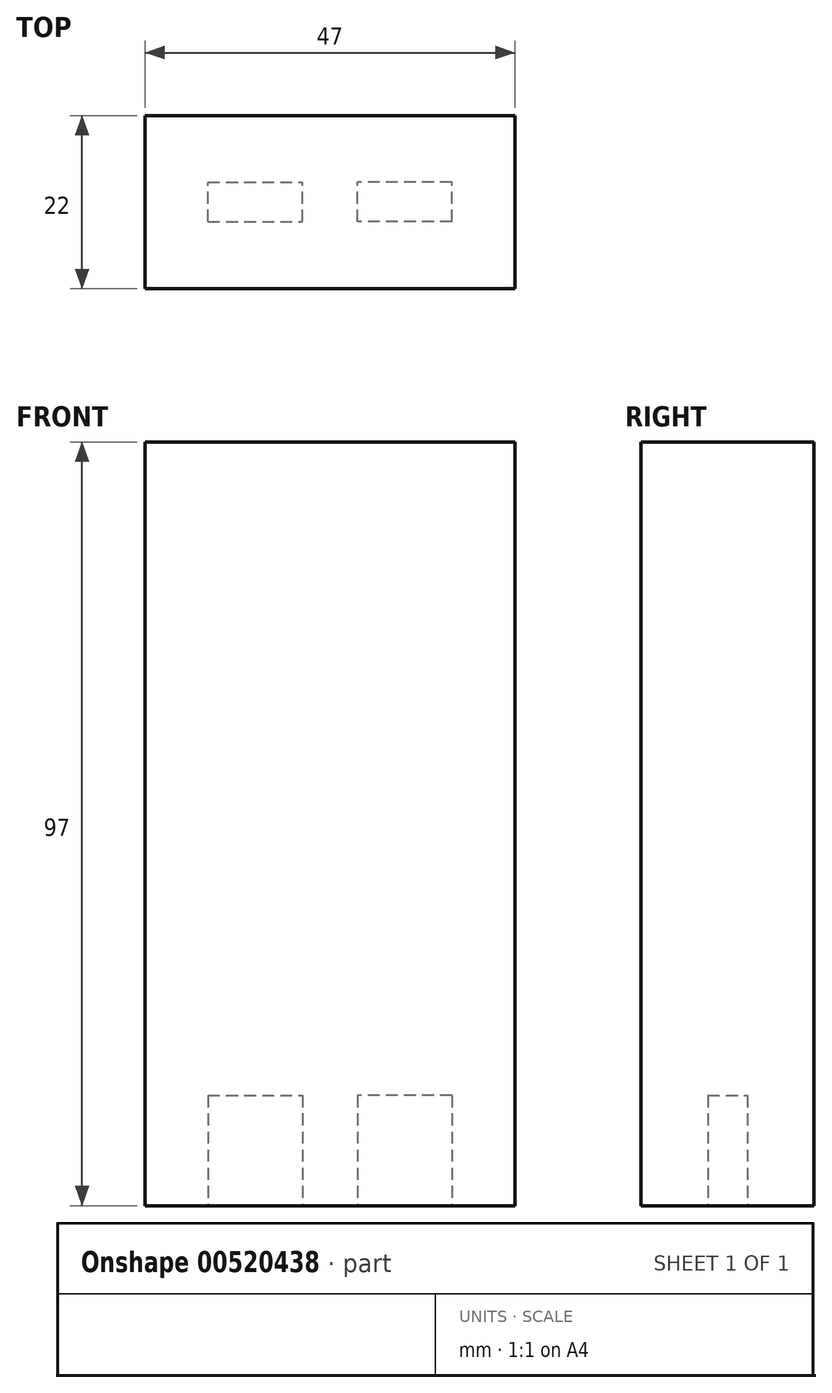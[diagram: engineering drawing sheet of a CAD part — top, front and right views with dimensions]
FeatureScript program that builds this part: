
annotation { "Feature Type Name" : "Feature", "Feature Type Description" : "" }
export const myFeature = defineFeature(function(context is Context, id is Id, definition is map)
    precondition{}
    {
        {
            var Q0;
            Q0=qCreatedBy(makeId("Front.planeOp"),FACE);
            var sketch = newSketch(context, id + "F0", { "sketchPlane" : qUnion([Q0])});
            skLineSegment(sketch, "E0.bottom", {"start": v(-41.2, 54.27) * mm, "end": v(5.8, 54.27) * mm});
            skLineSegment(sketch, "E0.top", {"start": v(-41.2, -42.73) * mm, "end": v(5.8, -42.73) * mm});
            skLineSegment(sketch, "E0.left", {"start": v(-41.2, 54.27) * mm, "end": v(-41.2, -42.73) * mm});
            skLineSegment(sketch, "E0.right", {"start": v(5.8, 54.27) * mm, "end": v(5.8, -42.73) * mm});
            skSolve(sketch);
        }
        {
            var Q0;
            Q0 = qSketchRegion(id + "F0", true);
            extrude(context, id + "F1", {"entities" : qUnion([Q0]), "depth" : 22 * mm, "offsetDistance" : 25 * mm});
        }
        {
            var Q0;
            Q0=makeQuery(id+"F1.opExtrude","SWEPT_FACE",FACE,{"disambiguationData":[OSD([sQuery(id+"F0.wireOp",EDGE,"E0.top")])]});
            var sketch = newSketch(context, id + "F2", { "sketchPlane" : qUnion([Q0])});
            skLineSegment(sketch, "E1.bottom", {"start": v(-33.2, 13.5) * mm, "end": v(-21.2, 13.5) * mm});
            skLineSegment(sketch, "E1.top", {"start": v(-33.2, 8.5) * mm, "end": v(-21.2, 8.5) * mm});
            skLineSegment(sketch, "E1.left", {"start": v(-33.2, 13.5) * mm, "end": v(-33.2, 8.5) * mm});
            skLineSegment(sketch, "E1.right", {"start": v(-21.2, 13.5) * mm, "end": v(-21.2, 8.5) * mm});
            skLineSegment(sketch, "E2", {"start": v(-41.2, 11) * mm, "end": v(5.8, 11) * mm, "construction": true});
            skLineSegment(sketch, "E3", {"start": v(-17.7, 22) * mm, "end": v(-17.7, 0) * mm, "construction": true});
            skLineSegment(sketch, "E4.MirrorCS", {"start": v(-14.2, 13.5) * mm, "end": v(-14.2, 8.5) * mm});
            skLineSegment(sketch, "E5.MirrorCS", {"start": v(-2.2, 8.5) * mm, "end": v(-14.2, 8.5) * mm});
            skLineSegment(sketch, "E6.MirrorCS", {"start": v(-2.2, 13.5) * mm, "end": v(-14.2, 13.5) * mm});
            skLineSegment(sketch, "E7.MirrorCS", {"start": v(-2.2, 13.5) * mm, "end": v(-2.2, 8.5) * mm});
            skSolve(sketch);
        }
        {
            var Q0;
            Q0 = qSketchRegion(id + "F2", true);
            extrude(context, id + "F3", {"entities" : qUnion([Q0]), "operationType" : NewBodyOperationType.REMOVE, "oppositeDirection" : true, "depth" : 14 * mm, "offsetDistance" : 25 * mm});
        }
    });
